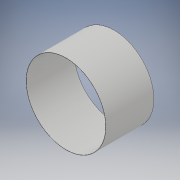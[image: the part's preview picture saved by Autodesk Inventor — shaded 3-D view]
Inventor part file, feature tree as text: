
AUTODESK INVENTOR PART (.ipt)
format: ipt  version: 2019 (Build 230136000, 136)  size: 102,912 bytes
history: native  units: mm
features: extrude x2, sketch x2
ambient origin geometry x8: Origin, YZ Plane, XZ Plane, XY Plane, X Axis, Y Axis, Z Axis, Center Point
bodies: Solid1 (feature_tree)
feature tree (4):
  extrude  "Extrusion1"  Depth=12.02mm TaperAngle=0.0deg
  extrude  "Extrusion2"  Depth=12.02mm TaperAngle=0.0deg
  sketch  "Sketch1"  dims[d0=19.97mm d1=12.02mm d2=0.0mm]
  sketch  "Sketch2"  dims[d3=19.87mm d4=12.02mm d5=0.0mm]
